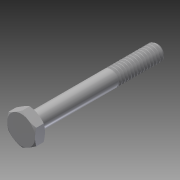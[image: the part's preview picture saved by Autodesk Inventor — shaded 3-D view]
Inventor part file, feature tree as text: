
AUTODESK INVENTOR PART (.ipt)
format: ipt  version: 2014 SP1 (Build 180222100, 222)  size: 530,944 bytes
history: native  units: in
note: dims shown in document units (in); Inventor stores cm internally (conversion verified against a paired STEP export)
features: extrude x1, other x1, imported_body x1
ambient origin geometry x8: Origin, YZ Plane, XZ Plane, XY Plane, X Axis, Y Axis, Z Axis, Center Point
bodies: Body1 (feature_tree)
feature tree (3):
  extrude  "Extrude14"  [1 undecoded]
  other  "91257A5501"
  imported_body  "Base1"
note: 1 required parameter value undecoded (feature->parameter linkage not recoverable at this tier; creation-order binding heuristic only, values carry confidence <= 0.55)
